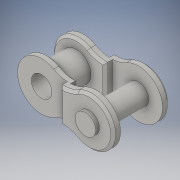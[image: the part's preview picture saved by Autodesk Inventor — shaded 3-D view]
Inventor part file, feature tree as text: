
AUTODESK INVENTOR PART (.ipt)
format: ipt  version: 2016 (Build 200138000, 138)  size: 188,928 bytes
history: native  units: in
note: dims shown in document units (in); Inventor stores cm internally (conversion verified against a paired STEP export)
features: extrude x5, sketch x5, plane x2, chamfer x2, mirror x2
ambient origin geometry x8: Origin, YZ Plane, XZ Plane, XY Plane, X Axis, Y Axis, Z Axis, Center Point
bodies: Solid1 (feature_tree)
feature tree (16):
  plane  "Work Plane1"
  extrude  "Extrusion1"  Depth=0.05in TaperAngle=0.0deg
  chamfer  "Chamfer1"  Distance=0.0167in Angle=45.0deg
  extrude  "Extrusion2"  Depth=0.13in TaperAngle=0.0deg
  mirror  "Mirror1"
  extrude  "Extrusion3"  Depth=0.05in TaperAngle=0.0deg
  plane  "Work Plane2"
  extrude  "Extrusion4"  Depth=0.4375in TaperAngle=0.0deg
  chamfer  "Chamfer2"  [1 undecoded]
  mirror  "Mirror2"
  extrude  "Extrusion5"  [1 undecoded]
  sketch  "Sketch1"  dims[d0=0.1438in d1=0.05in d2=0.0in d3=0.0167in d4=0.0167in d5=45.0deg]
  sketch  "Sketch2"  dims[d6=0.2375in d7=0.0in d8=0.13in d9=0.0in]
  sketch  "Sketch3"  dims[d10=0.1938in d11=0.05in d12=0.0in]
  sketch  "Sketch4"  dims[d13=0.0167in d14=0.0167in d15=45.0deg d16=0.4375in d17=0.0in]
  sketch  "Sketch5"
note: 2 required parameter values undecoded (feature->parameter linkage not recoverable at this tier; creation-order binding heuristic only, values carry confidence <= 0.55)
